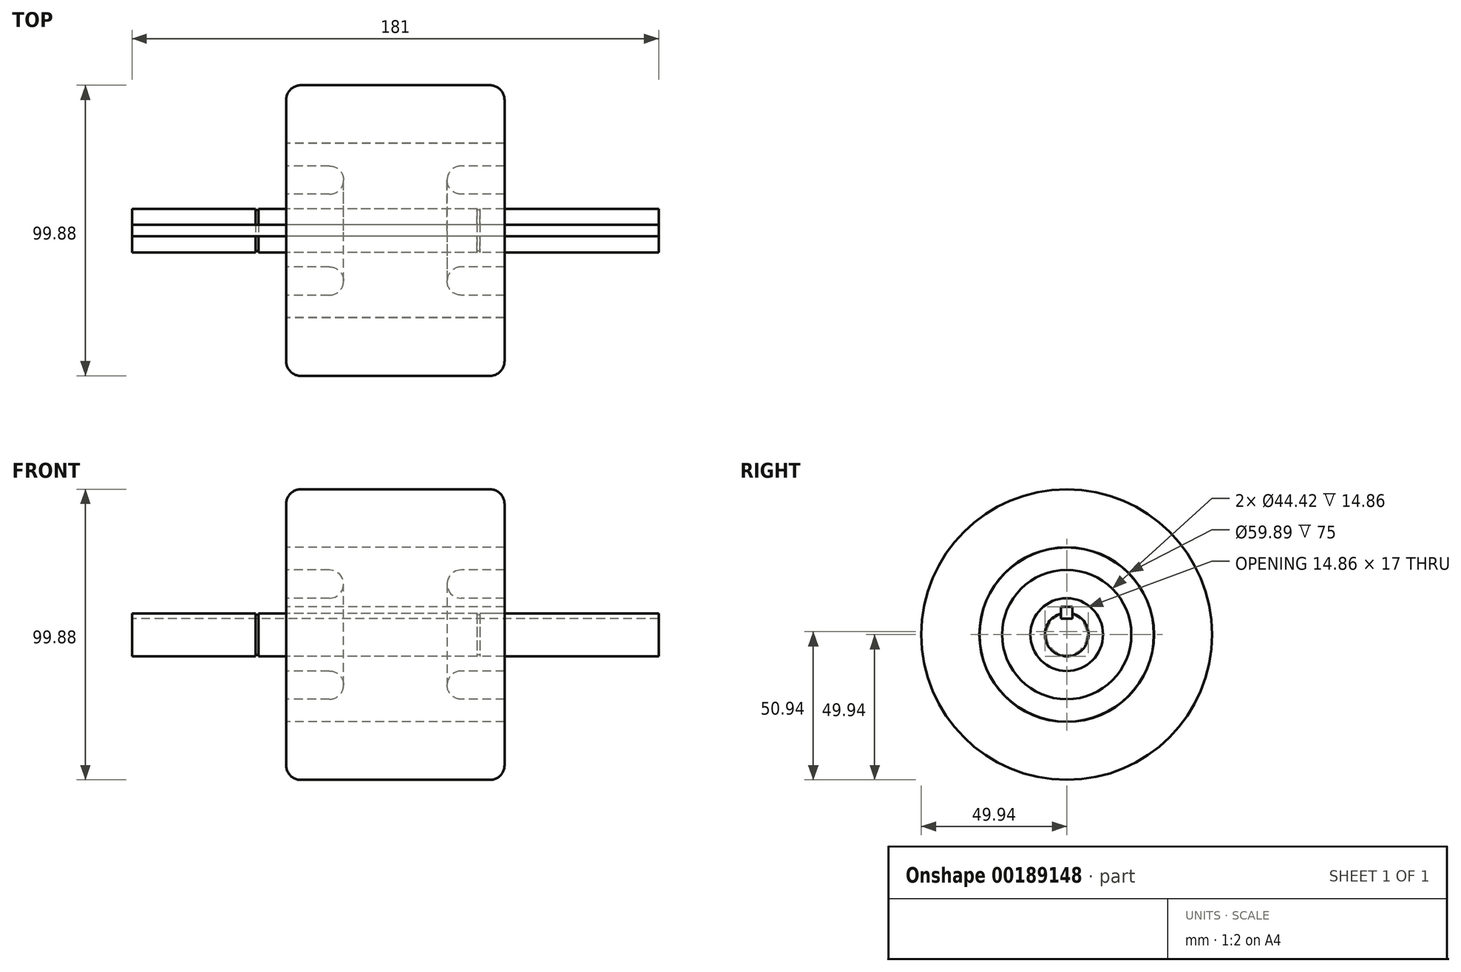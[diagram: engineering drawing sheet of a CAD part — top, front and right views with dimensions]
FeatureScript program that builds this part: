
annotation { "Feature Type Name" : "Feature", "Feature Type Description" : "" }
export const myFeature = defineFeature(function(context is Context, id is Id, definition is map)
    precondition{}
    {
        {
            var Q0;
            Q0=qCreatedBy(makeId("Front.planeOp"),FACE);
            var sketch = newSketch(context, id + "F0", { "sketchPlane" : qUnion([Q0])});
            skLineSegment(sketch, "E0", {"start": v(0, 0) * mm, "end": v(0, 7.5) * mm, "construction": true});
            skLineSegment(sketch, "E1", {"start": v(0, 7.5) * mm, "end": v(28, 7.5) * mm, "construction": true});
            skLineSegment(sketch, "E2", {"start": v(90.5, 7.5) * mm, "end": v(90.5, 0) * mm, "construction": true});
            skLineSegment(sketch, "E3", {"start": v(90.5, 0) * mm, "end": v(0, 0) * mm, "construction": true});
            skLineSegment(sketch, "E4.MirrorCS", {"start": v(0, 7.5) * mm, "end": v(-90.5, 7.5) * mm, "construction": true});
            skLineSegment(sketch, "E5.MirrorCS", {"start": v(-90.5, 7.5) * mm, "end": v(-90.5, 0) * mm, "construction": true});
            skLineSegment(sketch, "E6.MirrorCS", {"start": v(-90.5, 0) * mm, "end": v(0, 0) * mm, "construction": true});
            skLineSegment(sketch, "E7", {"start": v(-90.5, 0) * mm, "end": v(-90.5, 7.5) * mm});
            skLineSegment(sketch, "E8", {"start": v(90.5, 7.5) * mm, "end": v(90.5, 0) * mm});
            skLineSegment(sketch, "E9", {"start": v(-90.5, 7.5) * mm, "end": v(-48, 7.5) * mm});
            skLineSegment(sketch, "E10", {"start": v(-90.5, 0) * mm, "end": v(90.5, 0) * mm});
            skLineSegment(sketch, "E11", {"start": v(-9.5, 7.5) * mm, "end": v(-9.5, 0) * mm, "construction": true});
            skLineSegment(sketch, "E12", {"start": v(-47.5, 7.5) * mm, "end": v(-47.5, 0) * mm, "construction": true});
            skLineSegment(sketch, "E13", {"start": v(28.5, 7) * mm, "end": v(28.5, 0) * mm, "construction": true});
            skLineSegment(sketch, "E14", {"start": v(-48, 7.5) * mm, "end": v(-48, 7) * mm});
            skLineSegment(sketch, "E15", {"start": v(-48, 7) * mm, "end": v(-47, 7) * mm});
            skLineSegment(sketch, "E16", {"start": v(-47, 7) * mm, "end": v(-47, 7.5) * mm});
            skLineSegment(sketch, "E17.trimOffspring", {"start": v(-47, 7.5) * mm, "end": v(-10, 7.5) * mm});
            skLineSegment(sketch, "E18.trimOffspring", {"start": v(-9, 7.5) * mm, "end": v(28, 7.5) * mm});
            skLineSegment(sketch, "E19", {"start": v(-10, 7.5) * mm, "end": v(-9, 7.5) * mm});
            skLineSegment(sketch, "E20", {"start": v(28, 7.5) * mm, "end": v(28, 7) * mm});
            skLineSegment(sketch, "E21", {"start": v(28, 7) * mm, "end": v(29, 7) * mm});
            skLineSegment(sketch, "E22", {"start": v(29, 7) * mm, "end": v(29, 7.5) * mm});
            skLineSegment(sketch, "E23.trimOffspring", {"start": v(29, 7.5) * mm, "end": v(90.5, 7.5) * mm, "construction": true});
            skLineSegment(sketch, "E24.trimOffspring", {"start": v(29, 7.5) * mm, "end": v(90.5, 7.5) * mm});
            skPoint(sketch, "E25.orphan", {"position": v(28.5, 7.5) * mm});
            skSolve(sketch);
        }
        {
            var Q0;
            Q0 = qSketchRegion(id + "F0", true);
            var Q1;
            Q1=sQuery(id+"F0.wireOp",EDGE,"E10");
            revolve(context, id + "F1", {"entities" : qUnion([Q0]), "axis" : qUnion([Q1]), "revolveType" : RevolveType.FULL});
        }
        {
            var Q0;
            Q0=makeQuery(id+"F1.opRevolve","SWEPT_FACE",FACE,{"disambiguationData":[OSD([sQuery(id+"F0.wireOp",EDGE,"E7")])]});
            var sketch = newSketch(context, id + "F2", { "sketchPlane" : qUnion([Q0])});
            skLineSegment(sketch, "E26", {"start": v(0, 7.5) * mm, "end": v(0, 5.5) * mm, "construction": true});
            skLineSegment(sketch, "E27", {"start": v(0, 5.5) * mm, "end": v(2, 5.5) * mm, "construction": true});
            skLineSegment(sketch, "E28", {"start": v(2, 5.5) * mm, "end": v(2, 7.23) * mm, "construction": true});
            skLineSegment(sketch, "E29", {"start": v(0, 5.5) * mm, "end": v(-2, 5.5) * mm, "construction": true});
            skLineSegment(sketch, "E30", {"start": v(-2, 5.5) * mm, "end": v(-2, 7.23) * mm, "construction": true});
            skLineSegment(sketch, "E31", {"start": v(-2, 7.23) * mm, "end": v(-2, 5.5) * mm});
            skLineSegment(sketch, "E32", {"start": v(2, 5.5) * mm, "end": v(2, 7.23) * mm});
            skLineSegment(sketch, "E33", {"start": v(-2, 5.5) * mm, "end": v(2, 5.5) * mm});
            skLineSegment(sketch, "E34", {"start": v(-2, 5.5) * mm, "end": v(-2, 7.23) * mm});
            skSolve(sketch);
        }
        {
            var Q0;
            Q0=makeQuery(id+"F2.imprint","IMPRINT",FACE,{"disambiguationData":[TD([[makeQuery(id+"F2.imprint","IMPRINT",EDGE,{"derivedFrom":sQuery(id+"F2.wireOp",EDGE,"E33")}),1.0]])]});
            extrude(context, id + "F3", {"entities" : qUnion([Q0]), "operationType" : NewBodyOperationType.REMOVE, "endBound" : BoundingType.THROUGH_ALL, "oppositeDirection" : true, "depth" : 25 * mm});
        }
        {
            var Q0;
            Q0=qCreatedBy(makeId("Front.planeOp"),FACE);
            var sketch = newSketch(context, id + "F4", { "sketchPlane" : qUnion([Q0])});
            skLineSegment(sketch, "E35", {"start": v(0, 7.5) * mm, "end": v(37.5, 7.5) * mm});
            skLineSegment(sketch, "E36", {"start": v(37.5, 7.5) * mm, "end": v(37.5, 12.5) * mm});
            skLineSegment(sketch, "E37", {"start": v(37.5, 12.5) * mm, "end": v(22.64, 12.5) * mm});
            skLineSegment(sketch, "E38", {"start": v(0, 0) * mm, "end": v(0, 30) * mm, "construction": true});
            skArc(sketch, "E39", {"start": v(22.64, 22.21) * mm, "mid": v(17.78, 17.36) * mm, "end": v(22.64, 12.5) * mm});
            skLineSegment(sketch, "E40", {"start": v(37.5, 30) * mm, "end": v(37.5, 22.21) * mm});
            skLineSegment(sketch, "E41", {"start": v(37.5, 22.21) * mm, "end": v(22.64, 22.21) * mm});
            skLineSegment(sketch, "E42", {"start": v(0, 30) * mm, "end": v(37.5, 30) * mm});
            skLineSegment(sketch, "E43.MirrorCS", {"start": v(0, 30) * mm, "end": v(-37.5, 30) * mm});
            skLineSegment(sketch, "E44.MirrorCS", {"start": v(-37.5, 30) * mm, "end": v(-37.5, 22.21) * mm});
            skLineSegment(sketch, "E45.MirrorCS", {"start": v(-37.5, 22.21) * mm, "end": v(-22.64, 22.21) * mm});
            skArc(sketch, "E46.MirrorCS", {"start": v(-22.64, 22.21) * mm, "mid": v(-17.78, 17.36) * mm, "end": v(-22.64, 12.5) * mm});
            skLineSegment(sketch, "E47.MirrorCS", {"start": v(-37.5, 12.5) * mm, "end": v(-22.64, 12.5) * mm});
            skLineSegment(sketch, "E48.MirrorCS", {"start": v(-37.5, 7.5) * mm, "end": v(-37.5, 12.5) * mm});
            skLineSegment(sketch, "E49.MirrorCS", {"start": v(0, 7.5) * mm, "end": v(-37.5, 7.5) * mm});
            skSolve(sketch);
        }
        {
            var Q0;
            Q0=makeQuery(id+"F4.imprint","IMPRINT",FACE,{"disambiguationData":[TD([[makeQuery(id+"F4.imprint","IMPRINT",EDGE,{"derivedFrom":sQuery(id+"F4.wireOp",EDGE,"E35")}),1.0]])]});
            var Q1;
            Q1=sQuery(id+"F0.wireOp",EDGE,"E10");
            revolve(context, id + "F5", {"entities" : qUnion([Q0]), "axis" : qUnion([Q1]), "revolveType" : RevolveType.FULL});
        }
        {
            var Q0;
            Q0=makeQuery(id+"F5.opRevolve","SWEPT_FACE",FACE,{"disambiguationData":[OSD([sQuery(id+"F4.wireOp",EDGE,"E48.MirrorCS")])]});
            var sketch = newSketch(context, id + "F6", { "sketchPlane" : qUnion([Q0])});
            skLineSegment(sketch, "E50", {"start": v(0, 7.5) * mm, "end": v(0, 9.5) * mm, "construction": true});
            skLineSegment(sketch, "E51", {"start": v(0, 9.5) * mm, "end": v(0.2, 9.5) * mm, "construction": true});
            skLineSegment(sketch, "E52", {"start": v(2, 9.5) * mm, "end": v(0, 9.5) * mm, "construction": true});
            skLineSegment(sketch, "E53", {"start": v(0, 9.5) * mm, "end": v(-2, 9.5) * mm, "construction": true});
            skLineSegment(sketch, "E54", {"start": v(-2, 9.5) * mm, "end": v(2, 9.5) * mm});
            skLineSegment(sketch, "E55", {"start": v(2, 7.23) * mm, "end": v(2, 9.5) * mm});
            skLineSegment(sketch, "E56", {"start": v(-2, 9.5) * mm, "end": v(-2, 7.23) * mm});
            skSolve(sketch);
        }
        {
            var Q0;
            Q0 = qSketchRegion(id + "F6", true);
            var Q1;
            Q1=makeQuery(id+"F6.imprint","IMPRINT",FACE,{"disambiguationData":[TD([[makeQuery(id+"F6.imprint","IMPRINT",EDGE,{"derivedFrom":sQuery(id+"F6.wireOp",EDGE,"E54")}),-1.0]])]});
            extrude(context, id + "F7", {"entities" : qUnion([Q0, Q1]), "operationType" : NewBodyOperationType.REMOVE, "endBound" : BoundingType.THROUGH_ALL, "oppositeDirection" : true, "depth" : 25 * mm});
        }
        {
            var Q0;
            Q0=qCreatedBy(makeId("Front.planeOp"),FACE);
            var sketch = newSketch(context, id + "F8", { "sketchPlane" : qUnion([Q0])});
            skLineSegment(sketch, "E57", {"start": v(0, 29.94) * mm, "end": v(-37.5, 29.94) * mm});
            skLineSegment(sketch, "E58", {"start": v(-37.5, 29.94) * mm, "end": v(-37.5, 49.94) * mm});
            skLineSegment(sketch, "E59", {"start": v(-37.5, 49.94) * mm, "end": v(37.5, 49.94) * mm});
            skLineSegment(sketch, "E60", {"start": v(37.5, 49.94) * mm, "end": v(37.5, 29.94) * mm});
            skLineSegment(sketch, "E61", {"start": v(37.5, 29.94) * mm, "end": v(0, 29.94) * mm});
            skSolve(sketch);
        }
        {
            var Q0;
            Q0=makeQuery(id+"F8.imprint","IMPRINT",FACE,{"disambiguationData":[TD([[makeQuery(id+"F8.imprint","IMPRINT",EDGE,{"derivedFrom":sQuery(id+"F8.wireOp",EDGE,"E57")}),-1.0]])]});
            var Q1;
            Q1=sQuery(id+"F0.wireOp",EDGE,"E10");
            revolve(context, id + "F9", {"entities" : qUnion([Q0]), "axis" : qUnion([Q1]), "revolveType" : RevolveType.FULL});
        }
        {
            var Q0;
            Q0=makeQuery(id+"F9.opRevolve","SWEPT_EDGE",EDGE,{"disambiguationData":[OSD([sQuery(id+"F8.wireOp",EDGE,"E58"),sQuery(id+"F8.wireOp",EDGE,"E59")])]});
            var Q1;
            Q1=makeQuery(id+"F9.opRevolve","SWEPT_EDGE",EDGE,{"disambiguationData":[OSD([sQuery(id+"F8.wireOp",EDGE,"E59"),sQuery(id+"F8.wireOp",EDGE,"E60")])]});
            fillet(context, id + "F10", {"entities" : qUnion([Q0, Q1]), "radius" : 5 * mm, "tangentPropagation" : true, "allowEdgeOverflow" : false});
        }
    });
